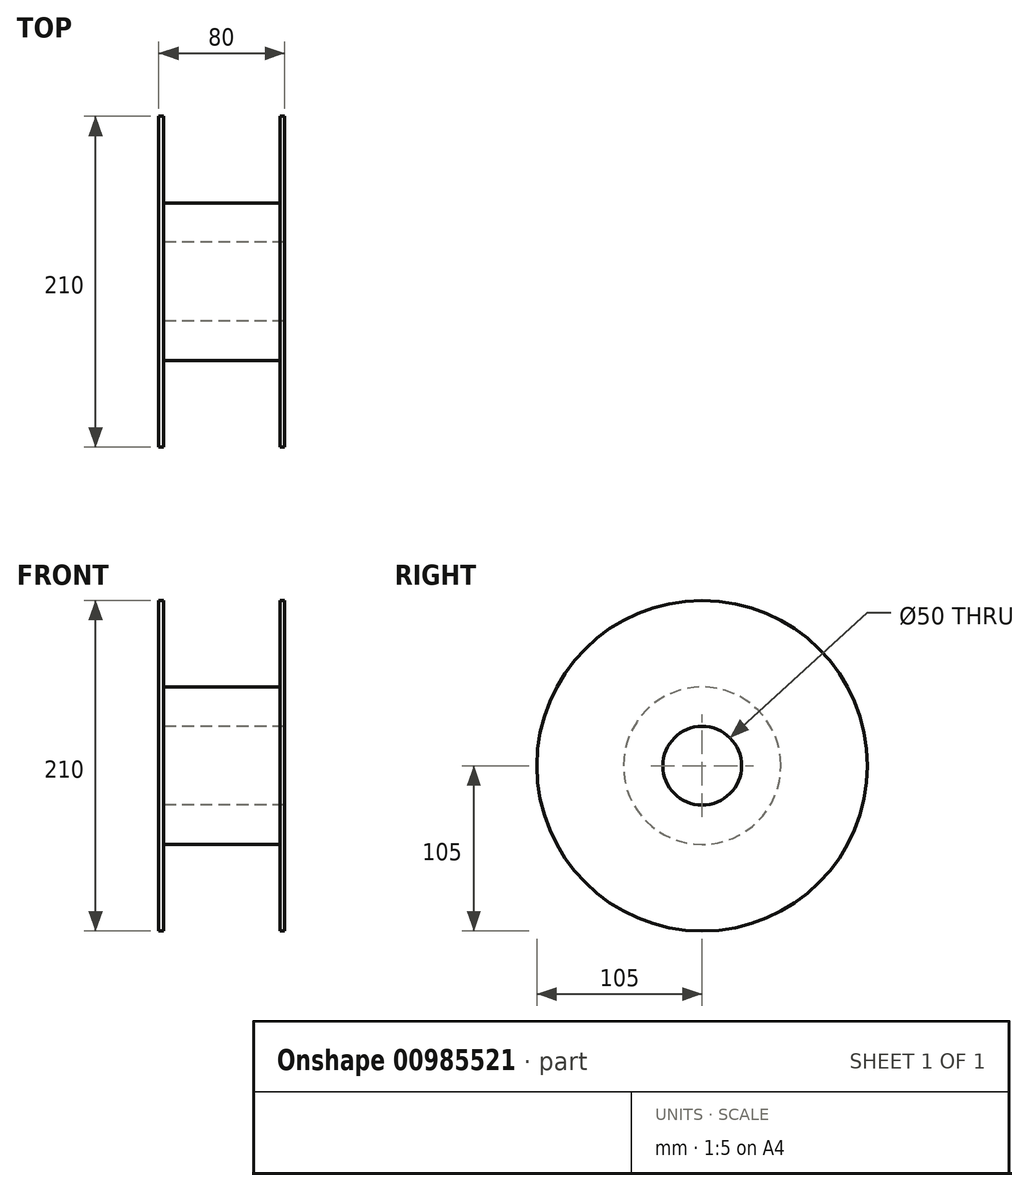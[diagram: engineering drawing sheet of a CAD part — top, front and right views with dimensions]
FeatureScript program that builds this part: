
annotation { "Feature Type Name" : "Feature", "Feature Type Description" : "" }
export const myFeature = defineFeature(function(context is Context, id is Id, definition is map)
    precondition{}
    {
        {
            var Q0;
            Q0=qCreatedBy(makeId("Front.planeOp"),FACE);
            var sketch = newSketch(context, id + "F0", { "sketchPlane" : qUnion([Q0])});
            skLineSegment(sketch, "E0", {"start": v(0, 105) * mm, "end": v(37, 105) * mm, "construction": true});
            skLineSegment(sketch, "E1", {"start": v(37, 105) * mm, "end": v(37, 50) * mm});
            skLineSegment(sketch, "E2", {"start": v(37, 50) * mm, "end": v(-37, 50) * mm});
            skLineSegment(sketch, "E3", {"start": v(-37, 50) * mm, "end": v(-37, 105) * mm});
            skLineSegment(sketch, "E4", {"start": v(-37, 105) * mm, "end": v(-40, 105) * mm});
            skLineSegment(sketch, "E5", {"start": v(-40, 105) * mm, "end": v(-40, 25) * mm});
            skLineSegment(sketch, "E6", {"start": v(-40, 25) * mm, "end": v(40, 25) * mm});
            skLineSegment(sketch, "E7", {"start": v(40, 25) * mm, "end": v(40, 105) * mm});
            skLineSegment(sketch, "E8", {"start": v(40, 105) * mm, "end": v(37, 105) * mm});
            skLineSegment(sketch, "E9", {"start": v(0, 105) * mm, "end": v(0, 0) * mm, "construction": true});
            skPoint(sketch, "E10", {"position": v(0, 105) * mm});
            skPoint(sketch, "E11", {"position": v(0, 25) * mm});
            skLineSegment(sketch, "E12", {"start": v(0, 0) * mm, "end": v(16.92, 0) * mm, "construction": true});
            skSolve(sketch);
        }
        {
            var Q0;
            Q0=makeQuery(id+"F0.imprint","IMPRINT",FACE,{"disambiguationData":[TD([[makeQuery(id+"F0.imprint","IMPRINT",EDGE,{"derivedFrom":sQuery(id+"F0.wireOp",EDGE,"E1")}),1.0]])]});
            var Q1;
            Q1=sQuery(id+"F0.wireOp",EDGE,"E12");
            revolve(context, id + "F1", {"surfaceOperationType" : NewSurfaceOperationType.NEW, "entities" : qUnion([Q0]), "axis" : qUnion([Q1]), "revolveType" : RevolveType.FULL});
        }
    });
